# Revit family: Thermostatic_Trim-GROHE-GrohTherm_SmartControl-29138_Series
name_source: partatom
category: Plumbing Fixtures
revit_build: Autodesk Revit 2018 (Build: 20170223_1515(x64)
units: mm (PartAtom-declared; Revit-internal decimal feet)

## family parameters
Cut with Voids When Loaded = No
Host = Face
OmniClass Number = 23.45.05.14.17
OmniClass Title = Showers
Part Type = Normal
Room Calculation Point = No
Round Connector Dimension = Use Diameter
Shared = Yes

## types (5) — shared parameters
Assembly Code = D2010710
CW Connection = Yes
CWFU = 3
Cold Water Connection Diameter = 1/2"
Cold Water Connection Radius = 1/4"
Default Elevation = 0"
Description = GrohTherm® SmartControl Triple Function Thermostatic Trim with Control Module
Diameter = 6 1/4"
Flow Rate = 9.5gpm (36L/min)
HW Connection = Yes
HWFU = 3
Hot Water Connection Diameter = 1"
Hot Water Connection Radius = 1/4"
IAPMO Compliance = ASME A112.18.1/CSA B125.1
Installation Type = Wall Mounted
Length = 1 11/16"
Manufacturer = Grohe
Operating Pressure = 43.5 psi (3 bar)
Price = Prices may vary. Please consult Manufacturer Representative for most up-to-date price list.
Product Documentation Link = https://americanstandard.box.com
Product Page URL = https://www.grohe.us
Revised Date = 05/27/2021
URL = https://www.grohe.us
Vent Connection = No
Warranty Documentation Link = https://cdn.cloud.grohe.com
Waste Connection = No
cUPC Compliant = Yes
zero-valued in all types: WFU

## per-type parameters (varying)
| type | Finish | Material |
| 29138000 | Metal-Grohe-000-StarLight Chrome | Metal-Grohe-000-StarLight Chrome |
| 29138EN0 | Metal-Grohe-EN0-Brushed Nickel Infinity Finish | Metal-Grohe-EN0-Brushed Nickel Infinity Finish |
| 29138A00 | Metal-Grohe-A00-Hard Graphite | Metal-Grohe-A00-Hard Graphite |
| 29138BE0 | Metal-Grohe-BE0-Polished Nickel Infinity Finish | Metal-Grohe-BE0-Polished Nickel Infinity Finish |
| 29138GN0 | Metal-Grohe-GN0-Brushed Cool Sunrise | Metal-Grohe-GN0-Brushed Cool Sunrise |

note: column(s) folded — value = type name in every type: Model

## geometry (parser evidence)
native form markers: Sweep x2
no freeform markers — native parametric forms only
